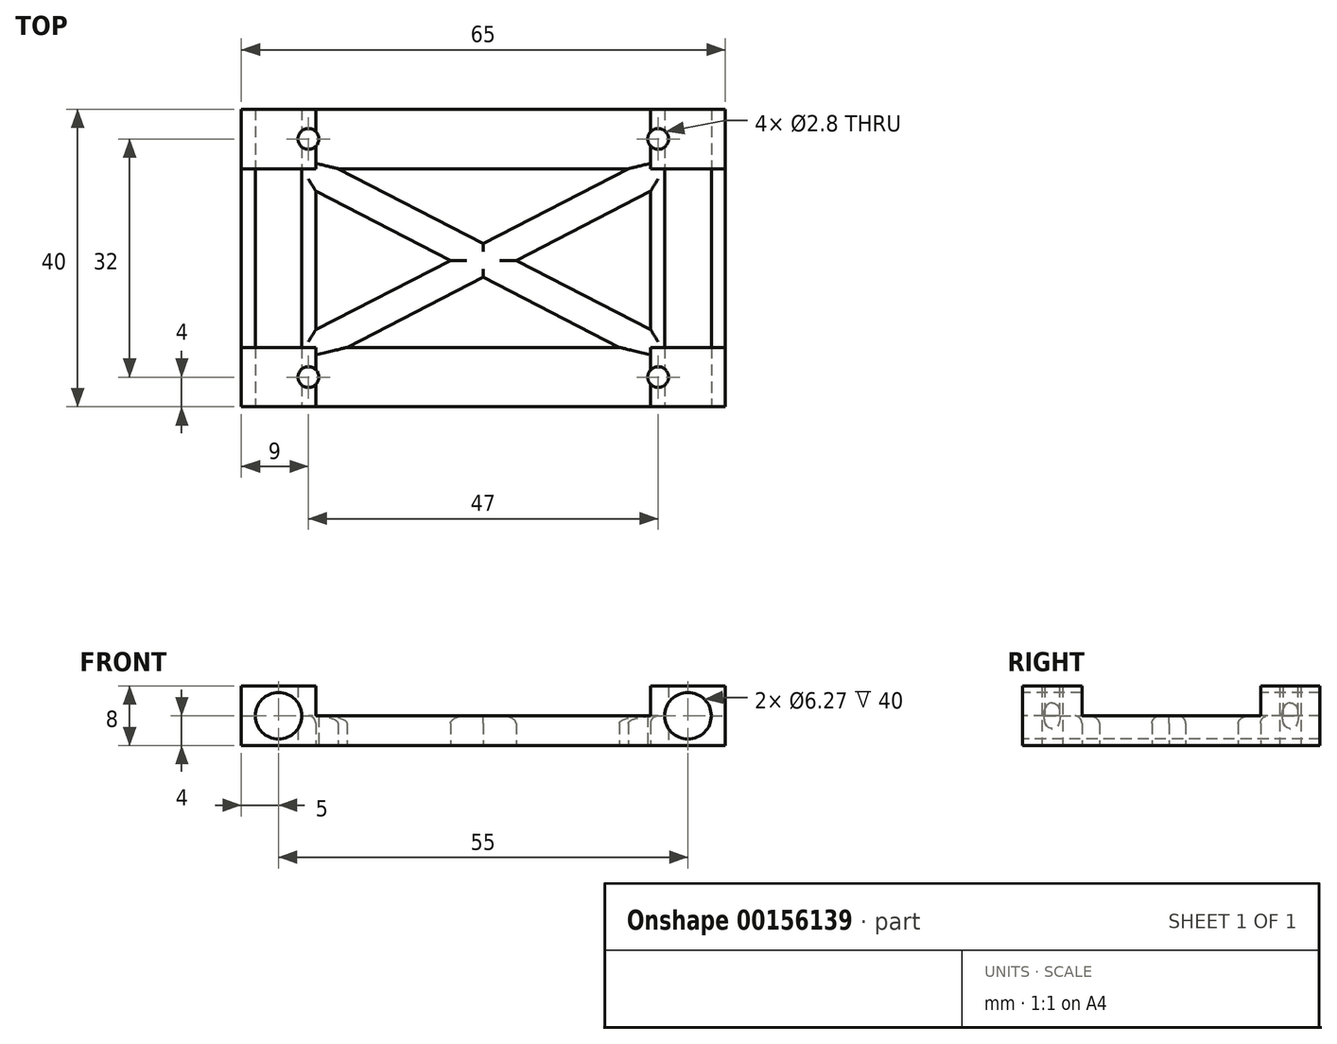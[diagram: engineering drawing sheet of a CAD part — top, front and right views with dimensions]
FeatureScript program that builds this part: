
annotation { "Feature Type Name" : "Feature", "Feature Type Description" : "" }
export const myFeature = defineFeature(function(context is Context, id is Id, definition is map)
    precondition{}
    {
        {
            var Q0;
            Q0=qCreatedBy(makeId("Top.planeOp"),FACE);
            var sketch = newSketch(context, id + "F0", { "sketchPlane" : qUnion([Q0])});
            skLineSegment(sketch, "E0.bottom", {"start": v(0, 0) * mm, "end": v(10, 0) * mm});
            skLineSegment(sketch, "E0.top", {"start": v(0, -8) * mm, "end": v(10, -8) * mm});
            skLineSegment(sketch, "E0.left", {"start": v(0, 0) * mm, "end": v(0, -8) * mm});
            skLineSegment(sketch, "E0.right", {"start": v(10, 0) * mm, "end": v(10, -8) * mm});
            skLineSegment(sketch, "E1.bottom", {"start": v(55, 0) * mm, "end": v(65, 0) * mm});
            skLineSegment(sketch, "E1.top", {"start": v(55, -8) * mm, "end": v(65, -8) * mm});
            skLineSegment(sketch, "E1.left", {"start": v(55, 0) * mm, "end": v(55, -8) * mm});
            skLineSegment(sketch, "E1.right", {"start": v(65, 0) * mm, "end": v(65, -8) * mm});
            skLineSegment(sketch, "E2.top", {"start": v(0, -40) * mm, "end": v(10, -40) * mm});
            skLineSegment(sketch, "E3.bottom", {"start": v(55, -32) * mm, "end": v(65, -32) * mm});
            skLineSegment(sketch, "E3.top", {"start": v(55, -40) * mm, "end": v(65, -40) * mm});
            skLineSegment(sketch, "E3.left", {"start": v(55, -32) * mm, "end": v(55, -40) * mm});
            skLineSegment(sketch, "E3.right", {"start": v(65, -32) * mm, "end": v(65, -40) * mm});
            skLineSegment(sketch, "E4.bottom", {"start": v(10, -8) * mm, "end": v(0, -8) * mm});
            skLineSegment(sketch, "E4.left", {"start": v(10, -11) * mm, "end": v(10, -29.63) * mm});
            skLineSegment(sketch, "E4.right", {"start": v(0, -8) * mm, "end": v(0, -40) * mm});
            skLineSegment(sketch, "E5.bottom", {"start": v(10, -40) * mm, "end": v(55, -40) * mm});
            skLineSegment(sketch, "E5.top", {"start": v(14.23, -32) * mm, "end": v(50.77, -32) * mm});
            skLineSegment(sketch, "E5.left", {"start": v(10, -40) * mm, "end": v(10, -32) * mm});
            skLineSegment(sketch, "E5.right", {"start": v(55, -40) * mm, "end": v(55, -32) * mm});
            skLineSegment(sketch, "E6.bottom", {"start": v(65, -8) * mm, "end": v(55, -8) * mm});
            skLineSegment(sketch, "E6.top", {"start": v(65, -32) * mm, "end": v(55, -32) * mm});
            skLineSegment(sketch, "E6.left", {"start": v(65, -8) * mm, "end": v(65, -32) * mm});
            skLineSegment(sketch, "E6.right", {"start": v(55, -11) * mm, "end": v(55, -29.63) * mm});
            skLineSegment(sketch, "E7.bottom", {"start": v(55, 0) * mm, "end": v(10, 0) * mm});
            skLineSegment(sketch, "E7.top", {"start": v(52, -8) * mm, "end": v(13, -8) * mm});
            skLineSegment(sketch, "E8", {"start": v(13, -8) * mm, "end": v(32.5, -18.04) * mm});
            skLineSegment(sketch, "E9", {"start": v(10, -11) * mm, "end": v(28.09, -20.32) * mm});
            skLineSegment(sketch, "E10", {"start": v(55, -11) * mm, "end": v(36.91, -20.32) * mm});
            skLineSegment(sketch, "E11", {"start": v(52, -8) * mm, "end": v(32.5, -18.04) * mm});
            skLineSegment(sketch, "E12.trimOffspring", {"start": v(28.09, -20.32) * mm, "end": v(10, -29.63) * mm});
            skLineSegment(sketch, "E13.trimOffspring", {"start": v(32.5, -22.59) * mm, "end": v(50.77, -32) * mm});
            skLineSegment(sketch, "E14.trimOffspring", {"start": v(32.5, -22.59) * mm, "end": v(14.23, -32) * mm});
            skLineSegment(sketch, "E15.trimOffspring", {"start": v(36.91, -20.32) * mm, "end": v(55, -29.63) * mm});
            skLineSegment(sketch, "E16", {"start": v(10, -32) * mm, "end": v(0, -32) * mm});
            skSolve(sketch);
        }
        {
            var Q0;
            Q0=makeQuery(id+"F0.imprint","IMPRINT",FACE,{"disambiguationData":[TD([[makeQuery(id+"F0.imprint","IMPRINT",EDGE,{"derivedFrom":sQuery(id+"F0.wireOp",EDGE,"E0.bottom")}),-1.0]])]});
            var Q1;
            Q1=makeQuery(id+"F0.imprint","IMPRINT",FACE,{"disambiguationData":[TD([[makeQuery(id+"F0.imprint","IMPRINT",EDGE,{"derivedFrom":sQuery(id+"F0.wireOp",EDGE,"E1.bottom")}),-1.0]])]});
            var Q2;
            Q2=makeQuery(id+"F0.imprint","IMPRINT",FACE,{"disambiguationData":[TD([[makeQuery(id+"F0.imprint","IMPRINT",EDGE,{"derivedFrom":sQuery(id+"F0.wireOp",EDGE,"E3.top")}),1.0]])]});
            var Q3;
            Q3=makeQuery(id+"F0.imprint","IMPRINT",FACE,{"disambiguationData":[TD([[makeQuery(id+"F0.imprint","IMPRINT",EDGE,{"derivedFrom":sQuery(id+"F0.wireOp",EDGE,"E2.top")}),1.0]])]});
            extrude(context, id + "F1", {"entities" : qUnion([Q0, Q1, Q2, Q3]), "depth" : 8 * mm});
        }
        {
            var Q0;
            Q0 = qSketchRegion(id + "F0", true);
            extrude(context, id + "F2", {"entities" : qUnion([Q0]), "operationType" : NewBodyOperationType.ADD, "depth" : 4 * mm});
        }
        {
            var Q0;
            Q0=makeQuery(id+"F1.opExtrude","SWEPT_FACE",FACE,{"disambiguationData":[OSD([sQuery(id+"F0.wireOp",EDGE,"E2.top")])]});
            var sketch = newSketch(context, id + "F3", { "sketchPlane" : qUnion([Q0])});
            skCircle(sketch, "E17", {"center": v(5, 4) * mm, "radius": 3.13 * mm});
            skCircle(sketch, "E18", {"center": v(60, 4) * mm, "radius": 3.13 * mm});
            skSolve(sketch);
        }
        {
            var Q0;
            Q0 = qSketchRegion(id + "F3", true);
            extrude(context, id + "F4", {"entities" : qUnion([Q0]), "operationType" : NewBodyOperationType.REMOVE, "endBound" : BoundingType.THROUGH_ALL, "oppositeDirection" : true, "depth" : 25 * mm});
        }
        {
            var Q0;
            Q0=makeQuery(id+"F2.opExtrude","CAP_EDGE",EDGE,{"disambiguationData":[OSD([sQuery(id+"F0.wireOp",EDGE,"E9")])],"isStart":false});
            var Q1;
            Q1=makeQuery(id+"F2.opExtrude","CAP_EDGE",EDGE,{"disambiguationData":[OSD([sQuery(id+"F0.wireOp",EDGE,"E12.trimOffspring")])],"isStart":false});
            var Q2;
            Q2=makeQuery(id+"F2.opExtrude","CAP_EDGE",EDGE,{"disambiguationData":[OSD([sQuery(id+"F0.wireOp",EDGE,"E4.left")])],"isStart":false});
            var Q3;
            Q3=makeQuery(id+"F2.opExtrude","CAP_EDGE",EDGE,{"disambiguationData":[OSD([sQuery(id+"F0.wireOp",EDGE,"E14.trimOffspring")])],"isStart":false});
            var Q4;
            Q4=makeQuery(id+"F2.opExtrude","CAP_EDGE",EDGE,{"disambiguationData":[OSD([sQuery(id+"F0.wireOp",EDGE,"E13.trimOffspring")])],"isStart":false});
            var Q5;
            Q5=makeQuery(id+"F2.opExtrude","CAP_EDGE",EDGE,{"disambiguationData":[OSD([sQuery(id+"F0.wireOp",EDGE,"E5.top")])],"isStart":false});
            var Q6;
            Q6=makeQuery(id+"F2.opExtrude","CAP_EDGE",EDGE,{"disambiguationData":[OSD([sQuery(id+"F0.wireOp",EDGE,"E15.trimOffspring")])],"isStart":false});
            var Q7;
            Q7=makeQuery(id+"F2.opExtrude","CAP_EDGE",EDGE,{"disambiguationData":[OSD([sQuery(id+"F0.wireOp",EDGE,"E10")])],"isStart":false});
            var Q8;
            Q8=makeQuery(id+"F2.opExtrude","CAP_EDGE",EDGE,{"disambiguationData":[OSD([sQuery(id+"F0.wireOp",EDGE,"E6.right")])],"isStart":false});
            var Q9;
            Q9=makeQuery(id+"F2.opExtrude","CAP_EDGE",EDGE,{"disambiguationData":[OSD([sQuery(id+"F0.wireOp",EDGE,"E7.top")])],"isStart":false});
            var Q10;
            Q10=makeQuery(id+"F2.opExtrude","CAP_EDGE",EDGE,{"disambiguationData":[OSD([sQuery(id+"F0.wireOp",EDGE,"E11")])],"isStart":false});
            var Q11;
            Q11=makeQuery(id+"F2.opExtrude","CAP_EDGE",EDGE,{"disambiguationData":[OSD([sQuery(id+"F0.wireOp",EDGE,"E8")])],"isStart":false});
            fillet(context, id + "F5", {"entities" : qUnion([Q0, Q1, Q2, Q3, Q4, Q5, Q6, Q7, Q8, Q9, Q10, Q11]), "radius" : 1 * mm, "tangentPropagation" : true, "allowEdgeOverflow" : false});
        }
        {
            var Q0;
            {var subQ0=sQuery(id+"F0.wireOp",EDGE,"E3.right");var subQ1=sQuery(id+"F0.wireOp",EDGE,"E3.top");var subQ2=sQuery(id+"F0.wireOp",EDGE,"E2.left");var subQ3=sQuery(id+"F0.wireOp",EDGE,"E2.top");var subQ4=sQuery(id+"F0.wireOp",EDGE,"E1.right");var subQ5=sQuery(id+"F0.wireOp",EDGE,"E1.bottom");var subQ6=sQuery(id+"F0.wireOp",EDGE,"E0.left");var subQ7=sQuery(id+"F0.wireOp",EDGE,"E0.bottom");Q0=makeQuery(id+"F2.boolean.opBoolean","MERGE",FACE,{"derivedFrom":[makeQuery(id+"F1.opExtrude","CAP_FACE",FACE,{"disambiguationData":[OSD([subQ7,subQ6,sQuery(id+"F0.wireOp",EDGE,"E4.bottom"),sQuery(id+"F0.wireOp",EDGE,"E0.right")])],"isStart":true}),makeQuery(id+"F1.opExtrude","CAP_FACE",FACE,{"disambiguationData":[OSD([subQ5,subQ4,sQuery(id+"F0.wireOp",EDGE,"E6.bottom"),sQuery(id+"F0.wireOp",EDGE,"E1.left")])],"isStart":true}),makeQuery(id+"F1.opExtrude","CAP_FACE",FACE,{"disambiguationData":[OSD([subQ3,subQ2,sQuery(id+"F0.wireOp",EDGE,"E4.top"),sQuery(id+"F0.wireOp",EDGE,"E5.left")])],"isStart":true}),makeQuery(id+"F1.opExtrude","CAP_FACE",FACE,{"disambiguationData":[OSD([subQ1,subQ0,sQuery(id+"F0.wireOp",EDGE,"E5.right"),sQuery(id+"F0.wireOp",EDGE,"E6.top")])],"isStart":true}),makeQuery(id+"F2.opExtrude","CAP_FACE",FACE,{"disambiguationData":[OSD([subQ7,subQ6,subQ5,subQ4,subQ3,subQ2,subQ1,subQ0,sQuery(id+"F0.wireOp",EDGE,"E4.left"),sQuery(id+"F0.wireOp",EDGE,"E4.right"),sQuery(id+"F0.wireOp",EDGE,"E5.bottom"),sQuery(id+"F0.wireOp",EDGE,"E5.top"),sQuery(id+"F0.wireOp",EDGE,"E6.left"),sQuery(id+"F0.wireOp",EDGE,"E6.right"),sQuery(id+"F0.wireOp",EDGE,"E7.bottom"),sQuery(id+"F0.wireOp",EDGE,"E7.top"),sQuery(id+"F0.wireOp",EDGE,"E8"),sQuery(id+"F0.wireOp",EDGE,"E9"),sQuery(id+"F0.wireOp",EDGE,"E10"),sQuery(id+"F0.wireOp",EDGE,"E11"),sQuery(id+"F0.wireOp",EDGE,"E12.trimOffspring"),sQuery(id+"F0.wireOp",EDGE,"E13.trimOffspring"),sQuery(id+"F0.wireOp",EDGE,"E14.trimOffspring"),sQuery(id+"F0.wireOp",EDGE,"E15.trimOffspring")])],"isStart":true})]});}
            var sketch = newSketch(context, id + "F6", { "sketchPlane" : qUnion([Q0])});
            skCircle(sketch, "E19", {"center": v(9, 36) * mm, "radius": 1.4 * mm});
            skCircle(sketch, "E20", {"center": v(56, 36) * mm, "radius": 1.4 * mm});
            skCircle(sketch, "E21", {"center": v(9, 4) * mm, "radius": 1.4 * mm});
            skCircle(sketch, "E22", {"center": v(56, 4) * mm, "radius": 1.4 * mm});
            skSolve(sketch);
        }
        {
            var Q0;
            Q0 = qSketchRegion(id + "F6", true);
            extrude(context, id + "F7", {"entities" : qUnion([Q0]), "operationType" : NewBodyOperationType.REMOVE, "oppositeDirection" : true, "depth" : 25 * mm});
        }
    });
